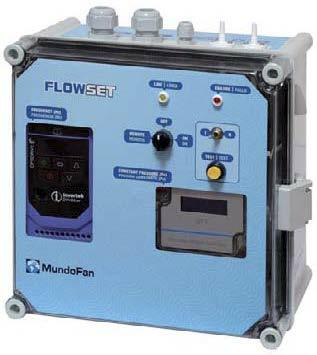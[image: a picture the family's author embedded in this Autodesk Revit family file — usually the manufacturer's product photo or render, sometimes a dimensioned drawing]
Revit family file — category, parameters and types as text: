
# Revit family: FLOWSET-22_VE10846
name_source: partatom
category: Aparatos eléctricos
revit_build: Autodesk Revit 2016 (Build: 20150220_1215(x64)
units: mm (PartAtom-declared; Revit-internal decimal feet)

## family parameters
Compartido = No
Corte con vacíos al cargar = No
Cota de conector redondo = Diámetro de uso
Mantener orientación de anotación = No
Número OmniClass = 23.80.00.00
Punto de cálculo de habitación = No
Se basa en plano de trabajo = No
Siempre vertical = Sí
Tipo de pieza = Caja de conexiones
Título OmniClass = Electric Power and Lighting

## types (1)
- FLOWSET
    Alimentación = 400Vac trifásico
    Corriente = 5,8 A
    Costo = 0 $
    Código de montaje = VE10846
    Descripción = CONTROL EFICIENCIA ENERGETICA PARA VENTILADORES - Caudal aire constante
    Dimensiones máx. = 270x300x170 mm
    Fabricante = SALVADOR ESCODA
    Imagen de tipo = flowset.jpg
    Leds = linea / fallo
    Modelo = FLOWSET 2,2kW
    Normativas = EN-ISO 14644-1:2000
    Potencia = 2,2 kW
    Regulación = Mediante sonda analógica de presión
    Salida = 400Vac trifásico
    Selector = 3 posiciones remoto / off / on
    URL = www.salvadorescoda.com
    Visualización = frecuencia (Hz) y presión (Pa)
